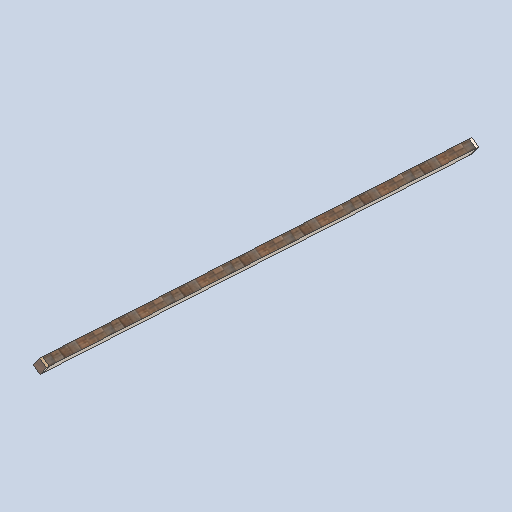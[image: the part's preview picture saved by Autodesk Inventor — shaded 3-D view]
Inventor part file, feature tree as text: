
AUTODESK INVENTOR PART (.ipt)
format: ipt  version: 2024.2 (Build 282272000, 272)  size: 311,808 bytes
history: native  units: mm
features: sketch x4, plane x2, extrude x2, projected_geometry x2, loft x1
ambient origin geometry x8: Origin, YZ Plane, XZ Plane, XY Plane, X Axis, Y Axis, Z Axis, Center Point
bodies: Solid1 (feature_tree)
feature tree (11):
  sketch  "Sketch1"  dims[d0=0.0mm d1=7900.0mm d2=0.0mm d3=90.0deg]
  plane  "Work Plane2"
  loft  "Loft1"
  sketch  "Sketch3"  dims[d8=50.0mm d9=0.0mm]
  sketch  "Sketch4"
  extrude  "Extrusion1"  Depth=50.0mm TaperAngle=0.0deg
  extrude  "Extrusion2"  [1 undecoded]
  plane  "Work Plane1"
  sketch  "Sketch2"  dims[d4=0.0mm d5=90.0deg d6=50.0mm d7=0.0mm]
  projected_geometry  "Projected Loop1"
  projected_geometry  "Projected Loop2"
note: 1 required parameter value undecoded (feature->parameter linkage not recoverable at this tier; creation-order binding heuristic only, values carry confidence <= 0.55)
